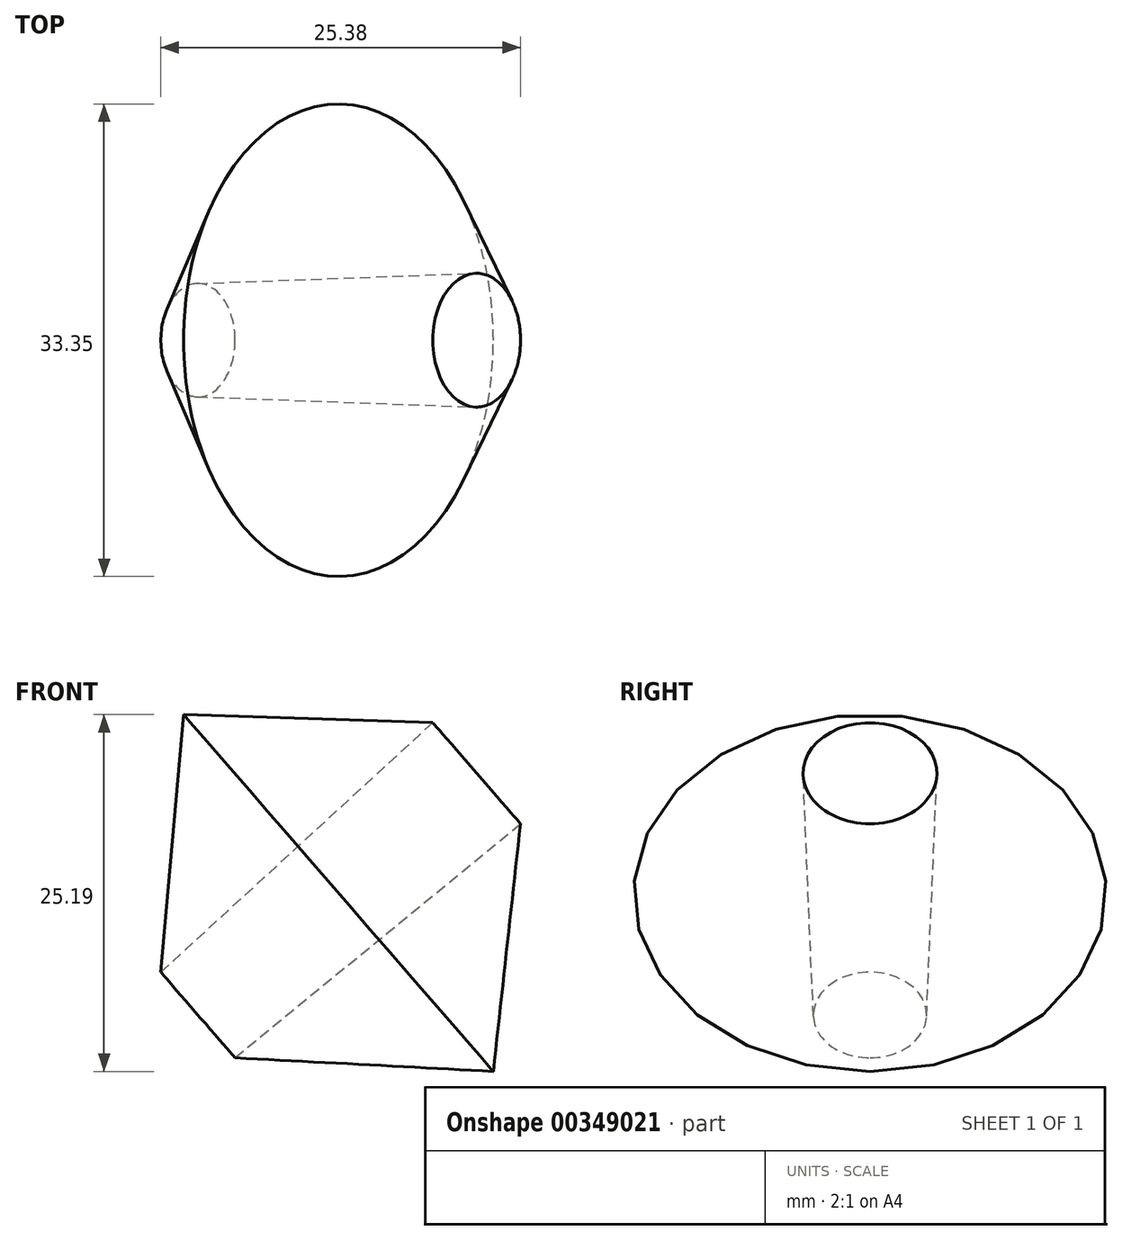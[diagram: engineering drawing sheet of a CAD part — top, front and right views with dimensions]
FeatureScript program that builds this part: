
annotation { "Feature Type Name" : "Feature", "Feature Type Description" : "" }
export const myFeature = defineFeature(function(context is Context, id is Id, definition is map)
    precondition{}
    {
        {
            var Q0;
            Q0=qCreatedBy(makeId("Front.planeOp"),FACE);
            var sketch = newSketch(context, id + "F0", { "sketchPlane" : qUnion([Q0])});
            skLineSegment(sketch, "E0", {"start": v(-6.2, 35.11) * mm, "end": v(-6.2, -14.52) * mm});
            skLineSegment(sketch, "E1", {"start": v(-6.2, -14.52) * mm, "end": v(-6.2, -14.52) * mm});
            skLineSegment(sketch, "E2", {"start": v(68.86, 46.13) * mm, "end": v(-6.2, -14.52) * mm});
            skLineSegment(sketch, "E3", {"start": v(-53.3, 10.13) * mm, "end": v(21.75, 21.14) * mm});
            skLineSegment(sketch, "E4", {"start": v(-55.98, 57.63) * mm, "end": v(0, 106.2) * mm});
            skLineSegment(sketch, "E5", {"start": v(0, 106.2) * mm, "end": v(-27.99, 81.91) * mm});
            skLineSegment(sketch, "E6", {"start": v(-27.99, 81.91) * mm, "end": v(-14, 94.06) * mm});
            skSolve(sketch);
        }
        {
            var Q0;
            Q0=sQuery(id+"F0.wireOp",EDGE,"E4");
            extrude(context, id + "F1", {"bodyType" : ToolBodyType.SURFACE, "surfaceEntities" : qUnion([Q0]), "depth" : 20.02 * mm});
        }
        {
            var Q0;
            Q0=makeQuery(id+"F1.opExtrude","SWEPT_FACE",FACE,{"disambiguationData":[OSD([sQuery(id+"F0.wireOp",EDGE,"E4")])]});
            var sketch = newSketch(context, id + "F2", { "sketchPlane" : qUnion([Q0])});
            skLineSegment(sketch, "E7", {"start": v(32.54, 20.02) * mm, "end": v(19.4, 7.34) * mm});
            skLineSegment(sketch, "E8", {"start": v(19.4, 7.34) * mm, "end": v(19.4, 7.34) * mm});
            skLineSegment(sketch, "E9", {"start": v(45.45, 8.06) * mm, "end": v(19.4, 7.34) * mm});
            skLineSegment(sketch, "E10", {"start": v(32.54, 20.02) * mm, "end": v(45.45, 8.06) * mm});
            skLineSegment(sketch, "E11", {"start": v(45.83, 3.34) * mm, "end": v(23.21, 3.34) * mm, "construction": true});
            skSolve(sketch);
        }
        {
            var Q0;
            Q0=makeQuery(id+"F2.imprint","IMPRINT",FACE,{"disambiguationData":[TD([[makeQuery(id+"F2.imprint","IMPRINT",EDGE,{"derivedFrom":sQuery(id+"F2.wireOp",EDGE,"E7")}),1.0]])]});
            var Q1;
            Q1=sQuery(id+"F2.wireOp",EDGE,"E11");
            revolve(context, id + "F3", {"entities" : qUnion([Q0]), "axis" : qUnion([Q1]), "revolveType" : RevolveType.FULL});
        }
    });
